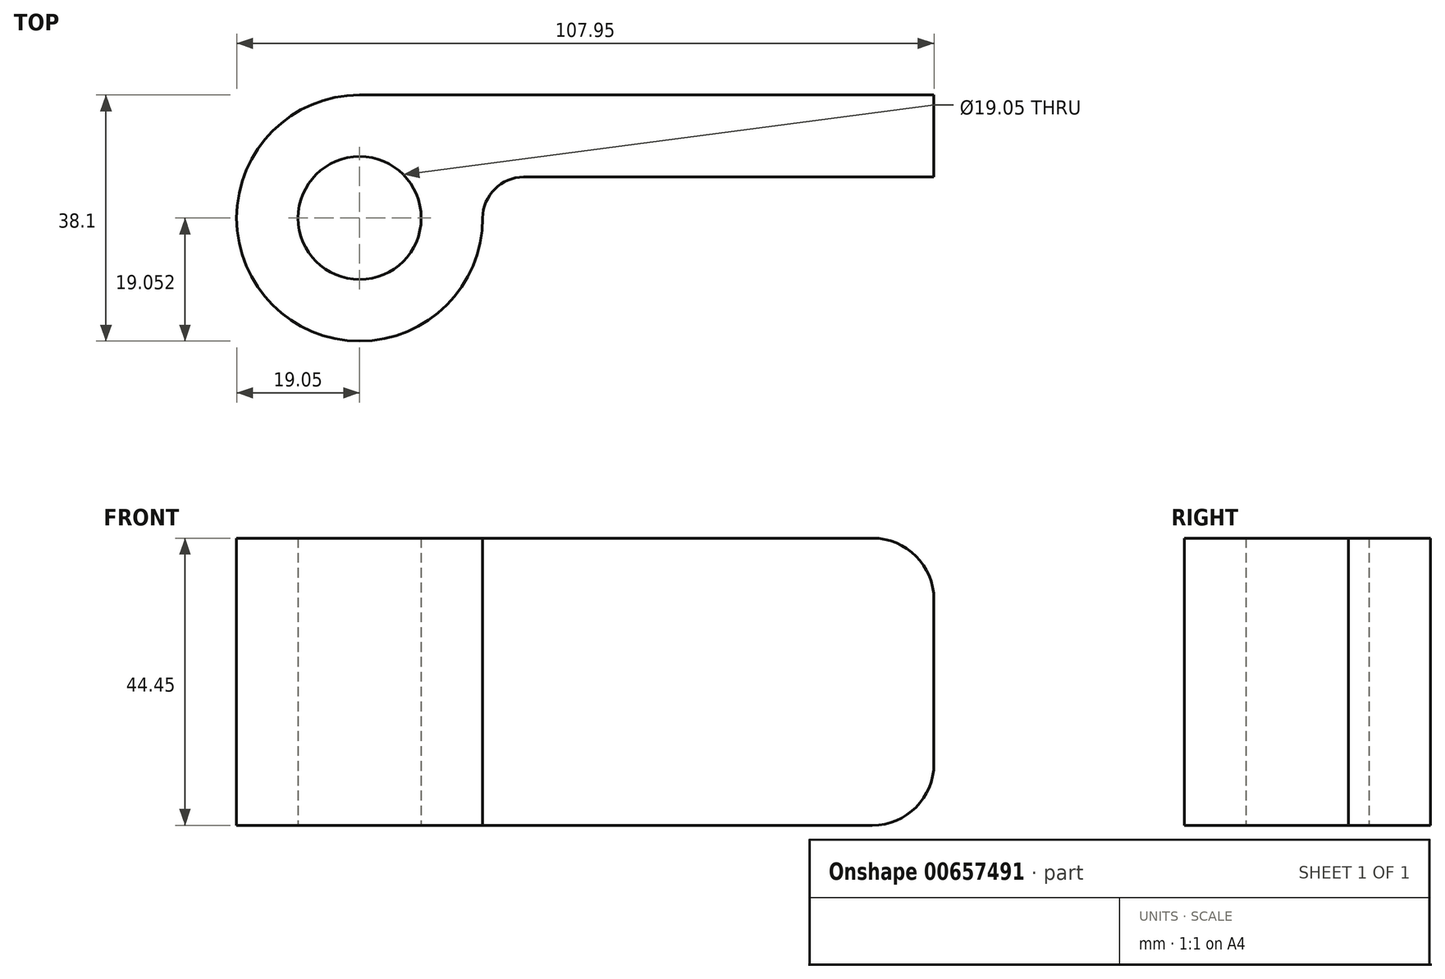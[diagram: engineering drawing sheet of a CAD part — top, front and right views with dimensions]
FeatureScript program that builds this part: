
annotation { "Feature Type Name" : "Feature", "Feature Type Description" : "" }
export const myFeature = defineFeature(function(context is Context, id is Id, definition is map)
    precondition{}
    {
        {
            var Q0;
            Q0=qCreatedBy(makeId("Top.planeOp"),FACE);
            var sketch = newSketch(context, id + "F0", { "sketchPlane" : qUnion([Q0])});
            skArc(sketch, "E0", {"start": v(-12.11, 23.81) * mm, "mid": v(-44.63, 37.28) * mm, "end": v(-31.16, 4.76) * mm});
            skCircle(sketch, "E1", {"center": v(-31.16, 23.81) * mm, "radius": 9.53 * mm});
            skPoint(sketch, "E2.start.orphan", {"position": v(-8.94, 23.81) * mm});
            skLineSegment(sketch, "E3", {"start": v(-12.11, 23.81) * mm, "end": v(-12.11, -65.09) * mm});
            skLineSegment(sketch, "E4", {"start": v(-12.11, -65.09) * mm, "end": v(-24.81, -65.09) * mm});
            skLineSegment(sketch, "E5", {"start": v(-24.81, -65.09) * mm, "end": v(-24.81, -1.59) * mm});
            skPoint(sketch, "E6.visualSharp", {"position": v(-24.81, 5.85) * mm});
            skArc(sketch, "E6.filletArc", {"start": v(-24.81, -1.59) * mm, "mid": v(-26.67, 2.9) * mm, "end": v(-31.16, 4.76) * mm});
            skSolve(sketch);
        }
        {
            var Q0;
            Q0 = qSketchRegion(id + "F0", true);
            extrude(context, id + "F1", {"entities" : qUnion([Q0]), "depth" : 44.45 * mm, "offsetDistance" : 25.4 * mm});
        }
        {
            var Q0;
            Q0=makeQuery(id+"F1.opExtrude","SWEPT_FACE",FACE,{"disambiguationData":[OSD([sQuery(id+"F0.wireOp",EDGE,"E5")])]});
            var sketch = newSketch(context, id + "F2", { "sketchPlane" : qUnion([Q0])});
            skLineSegment(sketch, "E7.bottom", {"start": v(1.59, 0) * mm, "end": v(55.56, 0) * mm});
            skLineSegment(sketch, "E7.top", {"start": v(1.59, 44.45) * mm, "end": v(55.56, 44.45) * mm});
            skLineSegment(sketch, "E7.left", {"start": v(1.59, 0) * mm, "end": v(1.59, 44.45) * mm});
            skLineSegment(sketch, "E7.right", {"start": v(65.09, 9.53) * mm, "end": v(65.09, 14.27) * mm});
            skPoint(sketch, "E8.visualSharp", {"position": v(65.09, 0) * mm});
            skArc(sketch, "E8.filletArc", {"start": v(55.56, 0) * mm, "mid": v(62.3, 2.79) * mm, "end": v(65.09, 9.53) * mm});
            skPoint(sketch, "E9.visualSharp", {"position": v(65.09, 44.45) * mm});
            skArc(sketch, "E9.filletArc", {"start": v(65.09, 34.93) * mm, "mid": v(62.3, 41.66) * mm, "end": v(55.56, 44.45) * mm});
            skLineSegment(sketch, "E10", {"start": v(65.09, 14.27) * mm, "end": v(14.29, 14.27) * mm});
            skLineSegment(sketch, "E11", {"start": v(14.29, 14.27) * mm, "end": v(65.09, 14.27) * mm});
            skLineSegment(sketch, "E12", {"start": v(65.09, 30.15) * mm, "end": v(14.29, 30.15) * mm});
            skLineSegment(sketch, "E13", {"start": v(14.29, 30.15) * mm, "end": v(65.09, 30.15) * mm});
            skArc(sketch, "E14", {"start": v(14.29, 30.15) * mm, "mid": v(6.35, 22.21) * mm, "end": v(14.29, 14.27) * mm});
            skLineSegment(sketch, "E15.trimOffspring", {"start": v(65.09, 30.15) * mm, "end": v(65.09, 34.93) * mm});
            skSolve(sketch);
        }
        {
            var Q0;
            {var subQ0=sQuery(id+"F2.wireOp",EDGE,"E11");Q0=makeQuery(id+"F2.imprint","IMPRINT",FACE,{"disambiguationData":[TD([[makeQuery(id+"F2.imprint","IMPRINT",EDGE,{"derivedFrom":subQ0}),1.0]])]});}
            var Q1;
            {var subQ0=sQuery(id+"F2.wireOp",EDGE,"E9.filletArc");Q1=makeQuery(id+"F2.imprint","IMPRINT",FACE,{"disambiguationData":[TD([[makeQuery(id+"F2.imprint","IMPRINT",EDGE,{"derivedFrom":subQ0}),-1.0]])]});}
            var Q2;
            {var subQ0=sQuery(id+"F2.wireOp",EDGE,"E8.filletArc");Q2=makeQuery(id+"F2.imprint","IMPRINT",FACE,{"disambiguationData":[TD([[makeQuery(id+"F2.imprint","IMPRINT",EDGE,{"derivedFrom":subQ0}),-1.0]])]});}
            extrude(context, id + "F3", {"entities" : qUnion([Q0, Q1, Q2]), "operationType" : NewBodyOperationType.REMOVE, "oppositeDirection" : true, "depth" : 25.4 * mm, "offsetDistance" : 25.4 * mm});
        }
        {
            var Q0;
            Q0=makeQuery(id+"F1.opExtrude","SWEPT_BODY",BODY,{"disambiguationData":[OSD([sQuery(id+"F0.wireOp",EDGE,"E0"),sQuery(id+"F0.wireOp",EDGE,"E1"),sQuery(id+"F0.wireOp",EDGE,"E3"),sQuery(id+"F0.wireOp",EDGE,"E4"),sQuery(id+"F0.wireOp",EDGE,"E5"),sQuery(id+"F0.wireOp",EDGE,"E6.filletArc")])]});
            var Q1;
            Q1=makeQuery(id+"F1.opExtrude","SWEPT_EDGE",EDGE,{"disambiguationData":[OSD([sQuery(id+"F0.wireOp",EDGE,"E0"),sQuery(id+"F0.wireOp",EDGE,"E3")])]});
            transform(context, id + "F4", {"entities" : qUnion([Q0]), "transformType" : TransformType.ROTATION, "transformAxis" : qUnion([Q1]), "angle" : 90 * degree, "oppositeDirection" : true, "makeCopy" : false});
        }
    });
